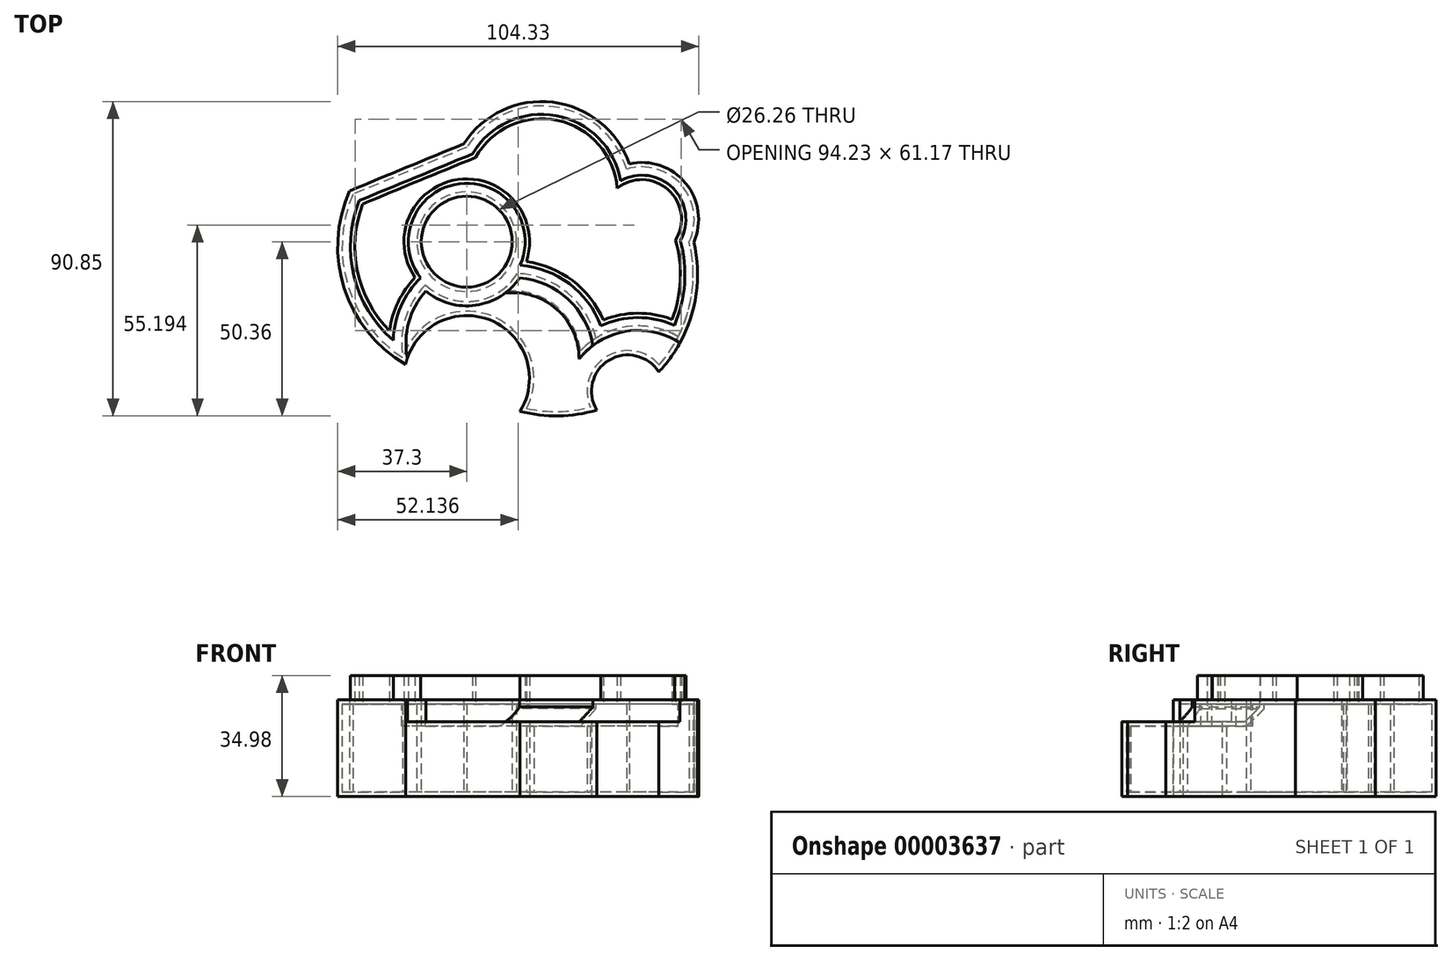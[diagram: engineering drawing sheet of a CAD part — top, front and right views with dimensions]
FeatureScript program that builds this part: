
annotation { "Feature Type Name" : "Feature", "Feature Type Description" : "" }
export const myFeature = defineFeature(function(context is Context, id is Id, definition is map)
    precondition{}
    {
        {
            var Q0;
            Q0=qCreatedBy(makeId("Top.planeOp"),FACE);
            var sketch = newSketch(context, id + "F0", { "sketchPlane" : qUnion([Q0])});
            skArc(sketch, "E0", {"start": v(0, 0) * mm, "mid": v(47.24, 13.63) * mm, "end": v(0, 27.27) * mm});
            skArc(sketch, "E1", {"start": v(0, 27.27) * mm, "mid": v(-32.9, 13.7) * mm, "end": v(-65.73, 0) * mm});
            skArc(sketch, "E2", {"start": v(-32.9, 13.7) * mm, "mid": v(-30.34, -21.48) * mm, "end": v(0, -39.48) * mm});
            skArc(sketch, "E3", {"start": v(0, -39.48) * mm, "mid": v(46.58, -43.24) * mm, "end": v(64.3, 0) * mm});
            skArc(sketch, "E4", {"start": v(46.17, 20.96) * mm, "mid": v(25.8, 44) * mm, "end": v(0, 27.27) * mm});
            skArc(sketch, "E5", {"start": v(64.3, 0) * mm, "mid": v(62.06, 16.38) * mm, "end": v(46.17, 20.96) * mm});
            skArc(sketch, "E6", {"start": v(8.69, 39.65) * mm, "mid": v(-31.64, 25.68) * mm, "end": v(-65.73, 0) * mm});
            skCircle(sketch, "E7", {"center": v(0, 0) * mm, "radius": 14.4 * mm});
            skCircle(sketch, "E8", {"center": v(46.58, -43.24) * mm, "radius": 11.78 * mm});
            skCircle(sketch, "E9", {"center": v(0, -39.48) * mm, "radius": 19.4 * mm});
            skSolve(sketch);
        }
        {
            var Q0;
            {var subQ4=sQuery(id+"F0.wireOp",EDGE,"E5");Q0=makeQuery(id+"F0.imprint","IMPRINT",FACE,{"disambiguationData":[TD([[makeQuery(id+"F0.imprint","IMPRINT",EDGE,{"derivedFrom":subQ4}),1.0]])]});}
            extrude(context, id + "F1", {"entities" : qUnion([Q0]), "depth" : 25.4 * mm});
        }
        {
            var Q0;
            Q0=makeQuery(id+"F1.opExtrude","CAP_FACE",FACE,{"disambiguationData":[OSD([sQuery(id+"F0.wireOp",EDGE,"E0"),sQuery(id+"F0.wireOp",EDGE,"E1"),sQuery(id+"F0.wireOp",EDGE,"E2"),sQuery(id+"F0.wireOp",EDGE,"E3"),sQuery(id+"F0.wireOp",EDGE,"E5"),sQuery(id+"F0.wireOp",EDGE,"E7"),sQuery(id+"F0.wireOp",EDGE,"E8"),sQuery(id+"F0.wireOp",EDGE,"E9")])],"isStart":false});
            var sketch = newSketch(context, id + "F2", { "sketchPlane" : qUnion([Q0])});
            skArc(sketch, "E10", {"start": v(61.15, -27.44) * mm, "mid": v(37.35, -27.86) * mm, "end": v(26.56, -49.08) * mm});
            skArc(sketch, "E11", {"start": v(37.35, -27.86) * mm, "mid": v(27.65, -13.68) * mm, "end": v(11.03, -9.26) * mm});
            skCircle(sketch, "E12", {"center": v(50.6, 6.47) * mm, "radius": 10.15 * mm});
            skLineSegment(sketch, "E13", {"start": v(50.6, 6.47) * mm, "end": v(50.6, -24.37) * mm});
            skArc(sketch, "E14", {"start": v(-9.78, -10.58) * mm, "mid": v(-17.3, -20.85) * mm, "end": v(-18.47, -33.53) * mm});
            skCircle(sketch, "E15.0", {"center": v(0, 0) * mm, "radius": 17.29 * mm});
            skSolve(sketch);
        }
        {
            var Q0;
            {var subQ1=sQuery(id+"F0.wireOp",EDGE,"E9");var subQ5=makeQuery(id+"F1.opExtrude","CAP_EDGE",EDGE,{"disambiguationData":[OSD([subQ1])],"isStart":false});Q0=makeQuery(id+"F2.imprint","IMPRINT",FACE,{"disambiguationData":[TD([[makeQuery(id+"F2.imprint","IMPRINT",EDGE,{"derivedFrom":subQ5}),-1.0]])]});}
            var Q1;
            {var subQ1=sQuery(id+"F0.wireOp",EDGE,"E8");var subQ5=makeQuery(id+"F1.opExtrude","CAP_EDGE",EDGE,{"disambiguationData":[OSD([subQ1])],"isStart":false});Q1=makeQuery(id+"F2.imprint","IMPRINT",FACE,{"disambiguationData":[TD([[makeQuery(id+"F2.imprint","IMPRINT",EDGE,{"derivedFrom":subQ5}),-1.0]])]});}
            extrude(context, id + "F3", {"entities" : qUnion([Q0, Q1]), "operationType" : NewBodyOperationType.REMOVE, "oppositeDirection" : true, "depth" : 6.35 * mm});
        }
        {
            var Q0;
            Q0=makeQuery(id+"F1.opExtrude","CAP_FACE",FACE,{"disambiguationData":[OSD([sQuery(id+"F0.wireOp",EDGE,"E0"),sQuery(id+"F0.wireOp",EDGE,"E1"),sQuery(id+"F0.wireOp",EDGE,"E2"),sQuery(id+"F0.wireOp",EDGE,"E3"),sQuery(id+"F0.wireOp",EDGE,"E5"),sQuery(id+"F0.wireOp",EDGE,"E7"),sQuery(id+"F0.wireOp",EDGE,"E8"),sQuery(id+"F0.wireOp",EDGE,"E9")])],"isStart":false});
            var sketch = newSketch(context, id + "F4", { "sketchPlane" : qUnion([Q0])});
            skArc(sketch, "E16.0", {"start": v(-14.55, -9.92) * mm, "mid": v(-19.72, -17.2) * mm, "end": v(-22.3, -25.75) * mm});
            skArc(sketch, "E16.1", {"start": v(-30.07, 10.9) * mm, "mid": v(-31.6, -8.58) * mm, "end": v(-22.3, -25.75) * mm});
            skArc(sketch, "E16.2", {"start": v(2.53, 24.33) * mm, "mid": v(-13.77, 17.63) * mm, "end": v(-30.07, 10.9) * mm});
            skArc(sketch, "E16.3", {"start": v(43.49, 15.46) * mm, "mid": v(26.3, 35.04) * mm, "end": v(2.53, 24.33) * mm});
            skArc(sketch, "E16.4", {"start": v(60.37, 0.46) * mm, "mid": v(58.22, 15.04) * mm, "end": v(43.49, 15.46) * mm});
            skArc(sketch, "E16.5", {"start": v(59.34, -22.5) * mm, "mid": v(61.74, -11.1) * mm, "end": v(60.37, 0.46) * mm});
            skArc(sketch, "E16.6", {"start": v(59.34, -22.5) * mm, "mid": v(49.39, -20.67) * mm, "end": v(39.47, -22.66) * mm});
            skArc(sketch, "E16.7", {"start": v(39.47, -22.66) * mm, "mid": v(29.6, -10.56) * mm, "end": v(14.84, -5.5) * mm});
            skCircle(sketch, "E17.0", {"center": v(0, 0) * mm, "radius": 18.15 * mm});
            skSolve(sketch);
        }
        {
            var Q0;
            {var subQ6=sQuery(id+"F4.wireOp",EDGE,"E16.1");Q0=makeQuery(id+"F4.imprint","IMPRINT",FACE,{"disambiguationData":[TD([[makeQuery(id+"F4.imprint","IMPRINT",EDGE,{"derivedFrom":subQ6}),1.0]])]});}
            extrude(context, id + "F5", {"entities" : qUnion([Q0]), "operationType" : NewBodyOperationType.ADD, "depth" : 8.3 * mm});
        }
        {
            var Q0;
            {var subQ0=sQuery(id+"F0.wireOp",EDGE,"E3");var subQ1=sQuery(id+"F0.wireOp",EDGE,"E8");var subQ2=sQuery(id+"F0.wireOp",EDGE,"E9");var subQ3=makeQuery(id+"F1.opExtrude","CAP_EDGE",EDGE,{"disambiguationData":[OSD([subQ0]),TDD([makeQuery(id+"F0.imprint","IMPRINT",EDGE,{"disambiguationData":[TD([[makeQuery(id+"F0.imprint","INTERSECT",VERTEX,{"derivedFrom":[subQ0,subQ2]}),-1.0]])],"derivedFrom":subQ0})])],"isStart":false});Q0=makeQuery(id+"F3.boolean.opBoolean","COPY",EDGE,{"derivedFrom":makeQuery(id+"F3.opExtrude","CAP_EDGE",EDGE,{"disambiguationData":[OSD([subQ0]),TDD([makeQuery(id+"F2.imprint","IMPRINT",EDGE,{"disambiguationData":[TD([[makeQuery(id+"F2.imprint","INTERSECT",VERTEX,{"derivedFrom":[subQ3,makeQuery(id+"F1.opExtrude","CAP_EDGE",EDGE,{"disambiguationData":[OSD([subQ2])],"isStart":false})]}),-1.0]])],"derivedFrom":subQ3}),makeQuery(id+"F2.imprint","IMPRINT",EDGE,{"disambiguationData":[TD([[makeQuery(id+"F2.imprint","INTERSECT",VERTEX,{"derivedFrom":[subQ3,makeQuery(id+"F1.opExtrude","CAP_EDGE",EDGE,{"disambiguationData":[OSD([subQ1])],"isStart":false})]}),1.0]])],"derivedFrom":subQ3})])],"isStart":false})});}
            var Q1;
            Q1=makeQuery(id+"F3.boolean.opBoolean","COPY",EDGE,{"derivedFrom":makeQuery(id+"F3.opExtrude","CAP_EDGE",EDGE,{"disambiguationData":[OSD([sQuery(id+"F2.wireOp",EDGE,"E11")])],"isStart":false})});
            var Q2;
            Q2=makeQuery(id+"F3.boolean.opBoolean","COPY",EDGE,{"derivedFrom":makeQuery(id+"F3.opExtrude","CAP_EDGE",EDGE,{"disambiguationData":[OSD([sQuery(id+"F0.wireOp",EDGE,"E8")])],"isStart":false})});
            var Q3;
            Q3=makeQuery(id+"F3.boolean.opBoolean","COPY",EDGE,{"derivedFrom":makeQuery(id+"F3.opExtrude","CAP_EDGE",EDGE,{"disambiguationData":[OSD([sQuery(id+"F0.wireOp",EDGE,"E9")])],"isStart":false})});
            var Q4;
            Q4=makeQuery(id+"F5.opExtrude","CAP_EDGE",EDGE,{"disambiguationData":[OSD([sQuery(id+"F4.wireOp",EDGE,"E16.7")])],"isStart":true});
            var Q5;
            Q5=makeQuery(id+"F5.opExtrude","CAP_EDGE",EDGE,{"disambiguationData":[OSD([sQuery(id+"F4.wireOp",EDGE,"E16.6")])],"isStart":true});
            var Q6;
            Q6=makeQuery(id+"F5.opExtrude","CAP_EDGE",EDGE,{"disambiguationData":[OSD([sQuery(id+"F4.wireOp",EDGE,"E16.0")])],"isStart":true});
            chamfer(context, id + "F6", {"entities" : qUnion([Q0, Q1, Q2, Q3, Q4, Q5, Q6]), "width" : 5.08 * mm, "tangentPropagation" : true});
        }
        {
            var Q0;
            Q0=qCreatedBy(makeId("Right.planeOp"),FACE);
            var sketch = newSketch(context, id + "F7", { "sketchPlane" : qUnion([Q0])});
            skCircle(sketch, "E18", {"center": v(0, 0) * mm, "radius": 3.38 * mm});
            skSolve(sketch);
        }
        {
            var Q0;
            Q0=makeQuery(id+"F5.opExtrude","CAP_FACE",FACE,{"disambiguationData":[OSD([sQuery(id+"F4.wireOp",EDGE,"E16.0"),sQuery(id+"F4.wireOp",EDGE,"E16.1"),sQuery(id+"F4.wireOp",EDGE,"E16.2"),sQuery(id+"F4.wireOp",EDGE,"E16.3"),sQuery(id+"F4.wireOp",EDGE,"E16.4"),sQuery(id+"F4.wireOp",EDGE,"E16.5"),sQuery(id+"F4.wireOp",EDGE,"E16.6"),sQuery(id+"F4.wireOp",EDGE,"E16.7"),sQuery(id+"F4.wireOp",EDGE,"E17.0")])],"isStart":false});
            shell(context, id + "F8", {"entities" : qUnion([Q0]), "thickness" : 1.27 * mm, "oppositeDirection" : true});
        }
    });
